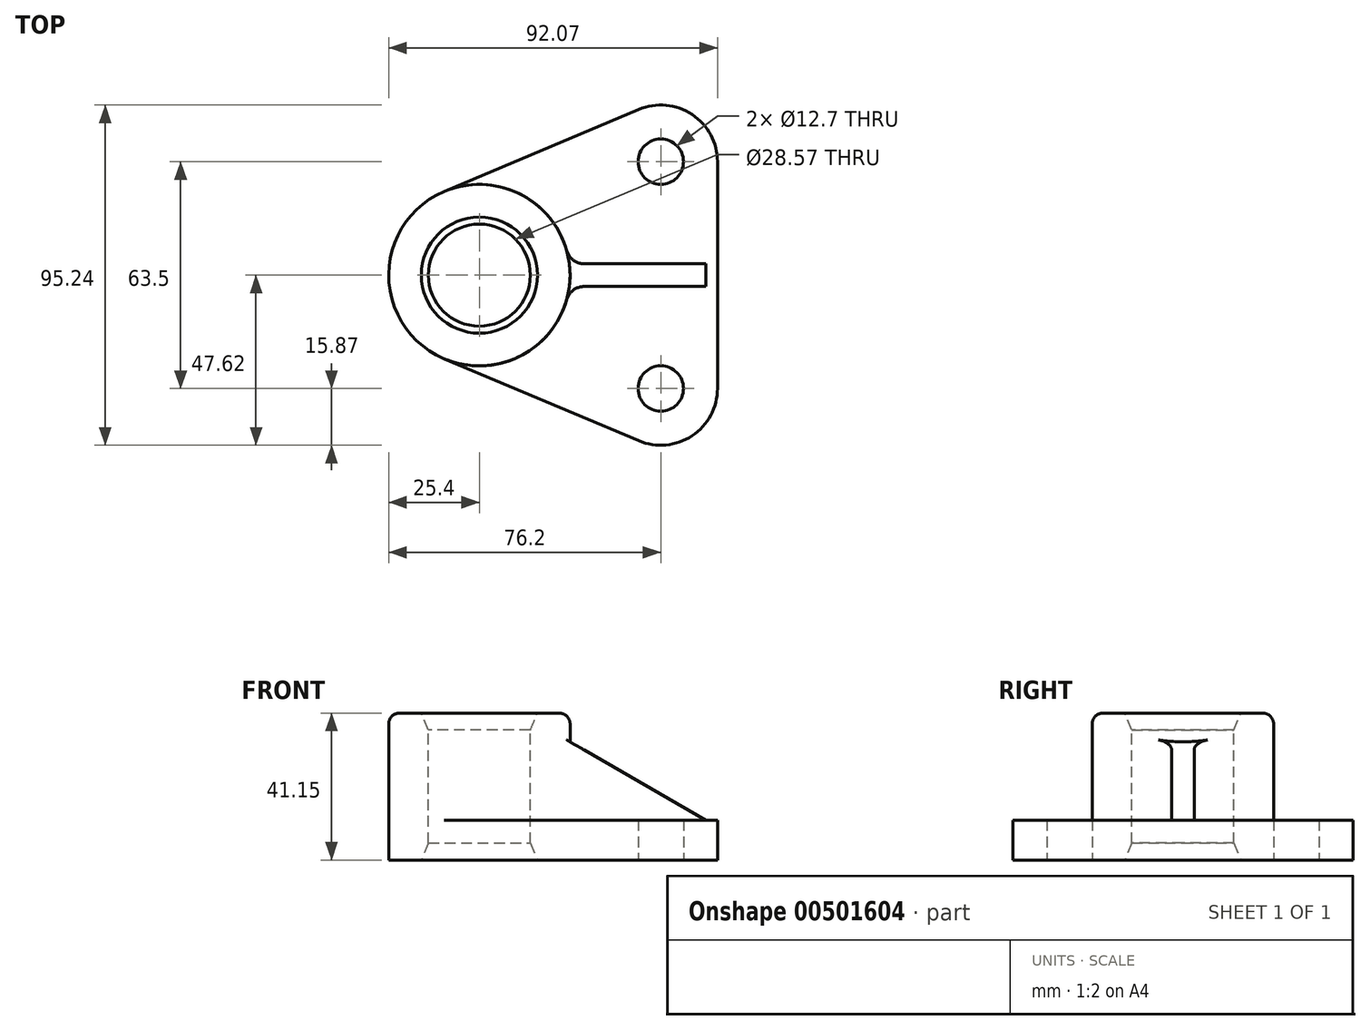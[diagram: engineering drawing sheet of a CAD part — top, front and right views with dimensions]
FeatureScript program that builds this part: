
annotation { "Feature Type Name" : "Feature", "Feature Type Description" : "" }
export const myFeature = defineFeature(function(context is Context, id is Id, definition is map)
    precondition{}
    {
        {
            var Q0;
            Q0=qCreatedBy(makeId("Top.planeOp"),FACE);
            var sketch = newSketch(context, id + "F0", { "sketchPlane" : qUnion([Q0])});
            skCircle(sketch, "E0", {"center": v(0, 0) * mm, "radius": 25.4 * mm});
            skArc(sketch, "E1", {"start": v(66.67, 31.75) * mm, "mid": v(59.58, 44.98) * mm, "end": v(44.63, 46.38) * mm});
            skArc(sketch, "E2", {"start": v(44.63, -46.38) * mm, "mid": v(59.58, -44.98) * mm, "end": v(66.68, -31.75) * mm});
            skLineSegment(sketch, "E3", {"start": v(-74.42, 0) * mm, "end": v(80.85, 0) * mm, "construction": true});
            skCircle(sketch, "E4", {"center": v(50.8, 31.75) * mm, "radius": 6.35 * mm});
            skCircle(sketch, "E5", {"center": v(50.8, -31.75) * mm, "radius": 6.35 * mm});
            skLineSegment(sketch, "E6", {"start": v(-9.87, 23.4) * mm, "end": v(44.63, 46.38) * mm});
            skLineSegment(sketch, "E7", {"start": v(-9.87, -23.4) * mm, "end": v(44.63, -46.38) * mm});
            skLineSegment(sketch, "E8", {"start": v(66.67, 31.75) * mm, "end": v(66.67, -31.75) * mm});
            skSolve(sketch);
        }
        {
            var Q0;
            {var subQ0=sQuery(id+"F0.wireOp",EDGE,"E0");var subQ1=makeQuery(id+"F0.imprint","INTERSECT",VERTEX,{"derivedFrom":[subQ0,sQuery(id+"F0.wireOp",EDGE,"E6")]});Q0=makeQuery(id+"F0.imprint","IMPRINT",FACE,{"disambiguationData":[TD([[makeQuery(id+"F0.imprint","IMPRINT",EDGE,{"disambiguationData":[TD([[subQ1,-1.0]])],"derivedFrom":subQ0}),1.0]])]});}
            extrude(context, id + "F1", {"entities" : qUnion([Q0]), "depth" : 41.15 * mm});
        }
        {
            var Q0;
            Q0=makeQuery(id+"F0.imprint","IMPRINT",FACE,{"disambiguationData":[TD([[makeQuery(id+"F0.imprint","IMPRINT",EDGE,{"derivedFrom":sQuery(id+"F0.wireOp",EDGE,"E1")}),1.0]])]});
            extrude(context, id + "F2", {"entities" : qUnion([Q0]), "operationType" : NewBodyOperationType.ADD, "depth" : 11.18 * mm});
        }
        {
            var Q0;
            Q0=makeQuery(id+"F1.opExtrude","CAP_FACE",FACE,{"disambiguationData":[OSD([sQuery(id+"F0.wireOp",EDGE,"E0")])],"isStart":false});
            var sketch = newSketch(context, id + "F3", { "sketchPlane" : qUnion([Q0])});
            skCircle(sketch, "E9", {"center": v(0, 0) * mm, "radius": 14.29 * mm});
            skSolve(sketch);
        }
        {
            var Q0;
            Q0 = qSketchRegion(id + "F3", true);
            extrude(context, id + "F4", {"entities" : qUnion([Q0]), "operationType" : NewBodyOperationType.REMOVE, "endBound" : BoundingType.THROUGH_ALL, "oppositeDirection" : true, "depth" : 25.4 * mm});
        }
        {
            var Q0;
            Q0=qCreatedBy(makeId("Front.planeOp"),FACE);
            var sketch = newSketch(context, id + "F5", { "sketchPlane" : qUnion([Q0])});
            skLineSegment(sketch, "E10.0", {"start": v(-9.87, 11.18) * mm, "end": v(25.4, 11.18) * mm});
            skLineSegment(sketch, "E11.0", {"start": v(63.37, 11.18) * mm, "end": v(66.68, 11.18) * mm});
            skLineSegment(sketch, "E12", {"start": v(22.46, 34.8) * mm, "end": v(63.37, 11.18) * mm});
            skPoint(sketch, "E13", {"position": v(63.37, 11.18) * mm});
            skLineSegment(sketch, "E14", {"start": v(22.46, 34.8) * mm, "end": v(22.46, 11.18) * mm});
            skPoint(sketch, "E15.orphan", {"position": v(44.63, 11.18) * mm});
            skLineSegment(sketch, "E16", {"start": v(22.46, 11.18) * mm, "end": v(63.37, 11.18) * mm});
            skSolve(sketch);
        }
        {
            var Q0;
            {var subQ0=sQuery(id+"F5.wireOp",EDGE,"E12");Q0=makeQuery(id+"F5.imprint","IMPRINT",FACE,{"disambiguationData":[TD([[makeQuery(id+"F5.imprint","IMPRINT",EDGE,{"derivedFrom":subQ0}),-1.0]])]});}
            extrude(context, id + "F6", {"entities" : qUnion([Q0]), "operationType" : NewBodyOperationType.ADD, "endBound" : BoundingType.SYMMETRIC, "depth" : 6.35 * mm});
        }
        {
            var Q0;
            Q0=makeQuery(id+"F1.opExtrude","CAP_FACE",FACE,{"disambiguationData":[OSD([sQuery(id+"F0.wireOp",EDGE,"E0")])],"isStart":false});
            var sketch = newSketch(context, id + "F7", { "sketchPlane" : qUnion([Q0])});
            skPoint(sketch, "E17", {"position": v(0, 0) * mm});
            skSolve(sketch);
        }
        {
            var Q0;
            Q0=sQuery(id+"F7.wireOp",VERTEX,"E17");
            var Q1;
            Q1=makeQuery(id+"F1.opExtrude","SWEPT_BODY",BODY,{"disambiguationData":[OSD([sQuery(id+"F0.wireOp",EDGE,"E0")])]});
            hole(context, id + "F8", {"style" : HoleStyle.C_SINK, "endStyle" : HoleEndStyle.THROUGH, "holeDiameter" : 28.57 * mm, "cSinkDiameter" : 32.5 * mm, "cSinkAngle" : 45 * degree, "isTappedThrough" : true, "tappedDepth" : 12.7 * mm, "tapClearance" : 3, "startFromSketch" : true, "locations" : qUnion([Q0]), "scope" : qUnion([Q1])});
        }
        {
            var Q0;
            {var subQ0=sQuery(id+"F0.wireOp",EDGE,"E0");Q0=makeQuery(id+"F2.boolean.opBoolean","MERGE",FACE,{"derivedFrom":[makeQuery(id+"F1.opExtrude","CAP_FACE",FACE,{"disambiguationData":[OSD([subQ0])],"isStart":true}),makeQuery(id+"F2.opExtrude","CAP_FACE",FACE,{"disambiguationData":[OSD([subQ0,sQuery(id+"F0.wireOp",EDGE,"E1"),sQuery(id+"F0.wireOp",EDGE,"E2"),sQuery(id+"F0.wireOp",EDGE,"E4"),sQuery(id+"F0.wireOp",EDGE,"E5"),sQuery(id+"F0.wireOp",EDGE,"E6"),sQuery(id+"F0.wireOp",EDGE,"E7"),sQuery(id+"F0.wireOp",EDGE,"E8")])],"isStart":true})]});}
            var sketch = newSketch(context, id + "F9", { "sketchPlane" : qUnion([Q0])});
            skPoint(sketch, "E18", {"position": v(0, 0) * mm});
            skSolve(sketch);
        }
        {
            var Q0;
            Q0=sQuery(id+"F9.wireOp",VERTEX,"E18");
            var Q1;
            Q1=makeQuery(id+"F1.opExtrude","SWEPT_BODY",BODY,{"disambiguationData":[OSD([sQuery(id+"F0.wireOp",EDGE,"E0")])]});
            hole(context, id + "F10", {"style" : HoleStyle.C_SINK, "endStyle" : HoleEndStyle.THROUGH, "holeDiameter" : 28.57 * mm, "cSinkDiameter" : 32.5 * mm, "cSinkAngle" : 45 * degree, "isTappedThrough" : true, "tappedDepth" : 12.7 * mm, "tapClearance" : 3, "startFromSketch" : true, "locations" : qUnion([Q0]), "scope" : qUnion([Q1])});
        }
        {
            var Q0;
            {var subQ0=sQuery(id+"F0.wireOp",EDGE,"E0");var subQ1=sQuery(id+"F0.wireOp",EDGE,"E7");Q0=makeQuery(id+"F6.boolean.opBoolean","SPLIT",EDGE,{"disambiguationData":[TD([makeQuery(id+"F2.opExtrude","SWEPT_FACE",FACE,{"disambiguationData":[OSD([subQ1])]})])],"derivedFrom":makeQuery(id+"F2.opExtrude","CAP_EDGE",EDGE,{"disambiguationData":[OSD([subQ0])],"isStart":false})});}
            var Q1;
            {var subQ0=sQuery(id+"F0.wireOp",EDGE,"E0");var subQ1=sQuery(id+"F0.wireOp",EDGE,"E6");Q1=makeQuery(id+"F6.boolean.opBoolean","SPLIT",EDGE,{"disambiguationData":[TD([makeQuery(id+"F2.opExtrude","SWEPT_FACE",FACE,{"disambiguationData":[OSD([subQ1])]})])],"derivedFrom":makeQuery(id+"F2.opExtrude","CAP_EDGE",EDGE,{"disambiguationData":[OSD([subQ0])],"isStart":false})});}
            var Q2;
            Q2=makeQuery(id+"F6.opExtrude","CAP_EDGE",EDGE,{"disambiguationData":[OSD([sQuery(id+"F5.wireOp",EDGE,"E16")])],"isStart":true});
            var Q3;
            Q3=makeQuery(id+"F6.boolean.opBoolean","INTERSECT",EDGE,{"derivedFrom":[makeQuery(id+"F1.opExtrude","SWEPT_FACE",FACE,{"disambiguationData":[OSD([sQuery(id+"F0.wireOp",EDGE,"E0")])]}),makeQuery(id+"F6.opExtrude","CAP_FACE",FACE,{"disambiguationData":[OSD([sQuery(id+"F5.wireOp",EDGE,"E12"),sQuery(id+"F5.wireOp",EDGE,"E14"),sQuery(id+"F5.wireOp",EDGE,"E16")])],"isStart":true})]});
            var Q4;
            Q4=makeQuery(id+"F6.boolean.opBoolean","INTERSECT",EDGE,{"derivedFrom":[makeQuery(id+"F1.opExtrude","SWEPT_FACE",FACE,{"disambiguationData":[OSD([sQuery(id+"F0.wireOp",EDGE,"E0")])]}),makeQuery(id+"F6.opExtrude","CAP_FACE",FACE,{"disambiguationData":[OSD([sQuery(id+"F5.wireOp",EDGE,"E12"),sQuery(id+"F5.wireOp",EDGE,"E14"),sQuery(id+"F5.wireOp",EDGE,"E16")])],"isStart":false})]});
            var Q5;
            Q5=makeQuery(id+"F6.opExtrude","CAP_EDGE",EDGE,{"disambiguationData":[OSD([sQuery(id+"F5.wireOp",EDGE,"E16")])],"isStart":false});
            fillet(context, id + "F11", {"entities" : qUnion([Q0, Q1, Q2, Q3, Q4, Q5]), "radius" : 5.08 * mm, "tangentPropagation" : true, "allowEdgeOverflow" : false});
        }
        {
            var Q0;
            Q0=makeQuery(id+"F1.opExtrude","CAP_EDGE",EDGE,{"disambiguationData":[OSD([sQuery(id+"F0.wireOp",EDGE,"E0")])],"isStart":false});
            fillet(context, id + "F12", {"entities" : qUnion([Q0]), "radius" : 3.05 * mm, "tangentPropagation" : true, "allowEdgeOverflow" : false});
        }
    });
